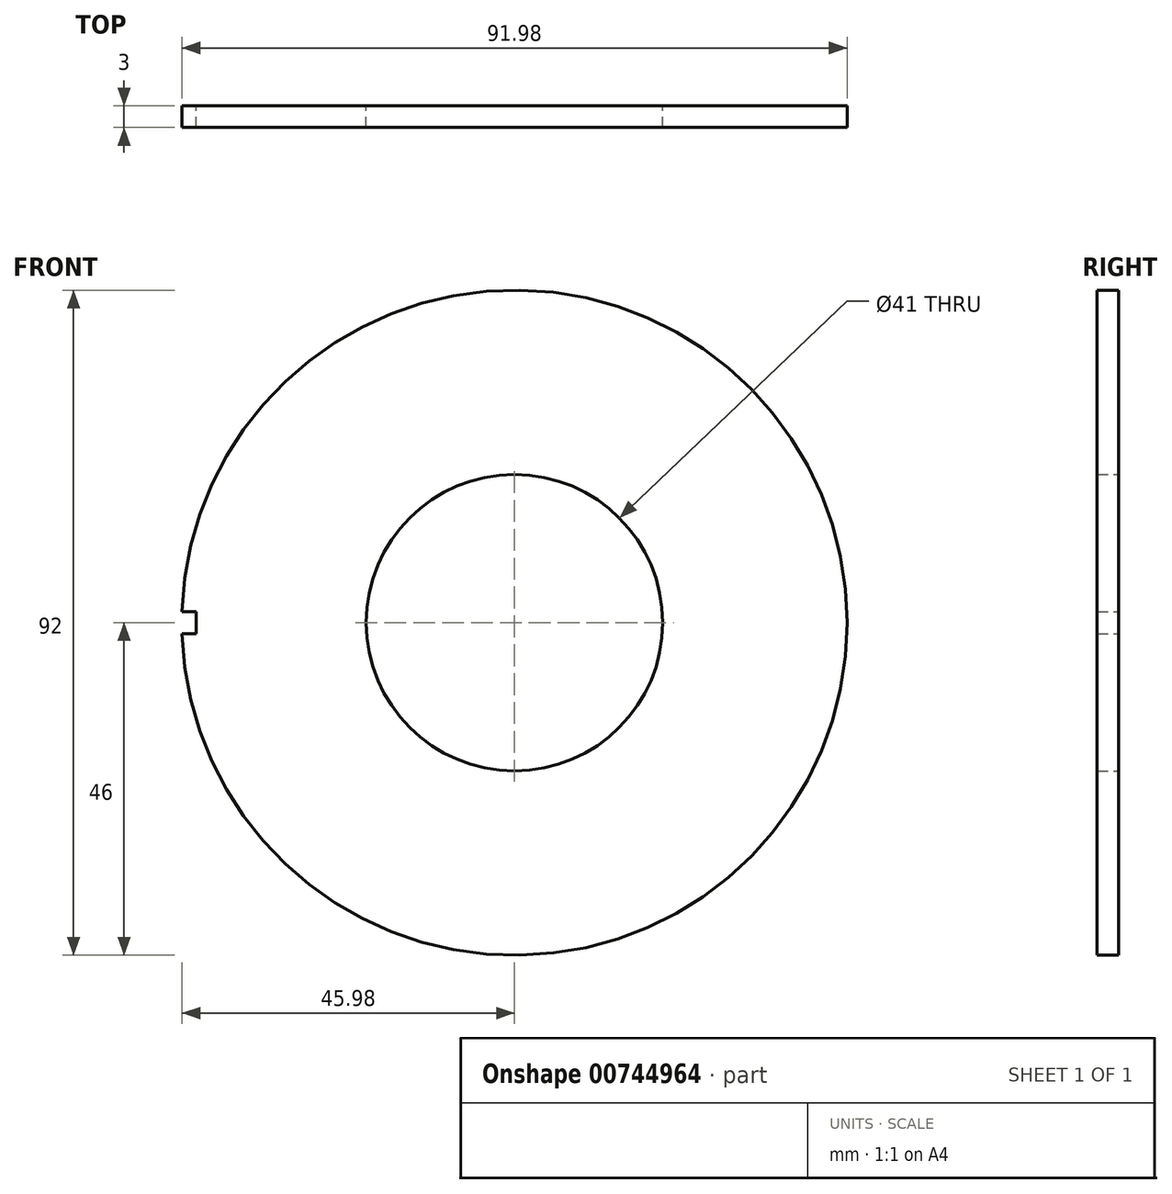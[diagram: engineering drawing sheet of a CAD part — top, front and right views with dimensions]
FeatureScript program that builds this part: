
annotation { "Feature Type Name" : "Feature", "Feature Type Description" : "" }
export const myFeature = defineFeature(function(context is Context, id is Id, definition is map)
    precondition{}
    {
        {
            var Q0;
            Q0=qCreatedBy(makeId("Front.planeOp"),FACE);
            var sketch = newSketch(context, id + "F0", { "sketchPlane" : qUnion([Q0])});
            skCircle(sketch, "E0", {"center": v(0, 0) * mm, "radius": 20.5 * mm});
            skCircle(sketch, "E1", {"center": v(0, 0) * mm, "radius": 46 * mm});
            skSolve(sketch);
        }
        {
            var Q0;
            Q0=makeQuery(id+"F0.imprint","IMPRINT",FACE,{"disambiguationData":[TD([[makeQuery(id+"F0.imprint","IMPRINT",EDGE,{"derivedFrom":sQuery(id+"F0.wireOp",EDGE,"E0")}),-1.0]])]});
            extrude(context, id + "F1", {"entities" : qUnion([Q0]), "depth" : 3 * mm, "offsetDistance" : 25 * mm});
        }
        {
            var Q0;
            Q0=qCreatedBy(makeId("Front.planeOp"),FACE);
            var sketch = newSketch(context, id + "F2", { "sketchPlane" : qUnion([Q0])});
            skLineSegment(sketch, "E2.bottom", {"start": v(-44, -1.5) * mm, "end": v(-46, -1.5) * mm});
            skLineSegment(sketch, "E2.top", {"start": v(-44, 1.5) * mm, "end": v(-46, 1.5) * mm});
            skLineSegment(sketch, "E2.left", {"start": v(-44, -1.5) * mm, "end": v(-44, 1.5) * mm});
            skLineSegment(sketch, "E2.right", {"start": v(-46, -1.5) * mm, "end": v(-46, 1.5) * mm});
            skPoint(sketch, "E2.middle", {"position": v(-45, 0) * mm});
            skSolve(sketch);
        }
        {
            var Q0;
            Q0 = qSketchRegion(id + "F2", true);
            extrude(context, id + "F3", {"entities" : qUnion([Q0]), "operationType" : NewBodyOperationType.REMOVE, "depth" : 3 * mm, "offsetDistance" : 25 * mm});
        }
    });
